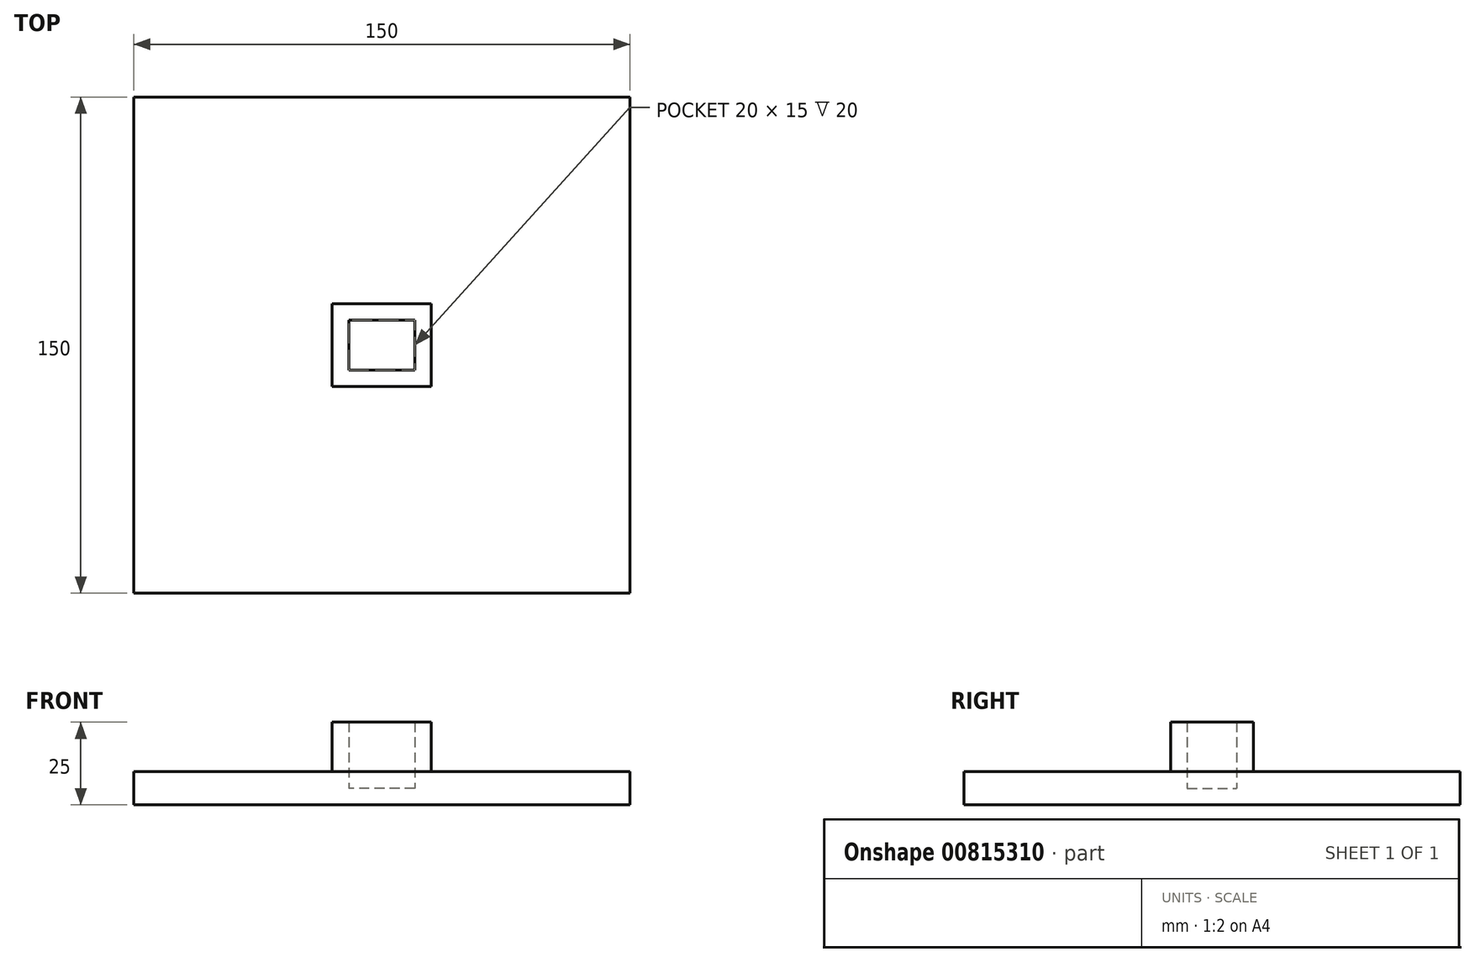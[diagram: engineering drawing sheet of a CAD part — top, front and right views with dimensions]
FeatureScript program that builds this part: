
annotation { "Feature Type Name" : "Feature", "Feature Type Description" : "" }
export const myFeature = defineFeature(function(context is Context, id is Id, definition is map)
    precondition{}
    {
        {
            var Q0;
            Q0=qCreatedBy(makeId("Top.planeOp"),FACE);
            var sketch = newSketch(context, id + "F0", { "sketchPlane" : qUnion([Q0])});
            skLineSegment(sketch, "E0.bottom", {"start": v(42.35, 98.82) * mm, "end": v(192.35, 98.82) * mm});
            skLineSegment(sketch, "E0.top", {"start": v(42.35, -51.18) * mm, "end": v(192.35, -51.18) * mm});
            skLineSegment(sketch, "E0.left", {"start": v(42.35, 98.82) * mm, "end": v(42.35, -51.18) * mm});
            skLineSegment(sketch, "E0.right", {"start": v(192.35, 98.82) * mm, "end": v(192.35, -51.18) * mm});
            skLineSegment(sketch, "E1", {"start": v(42.35, 98.82) * mm, "end": v(192.35, -51.18) * mm});
            skLineSegment(sketch, "E2", {"start": v(192.35, 98.82) * mm, "end": v(42.35, -51.18) * mm});
            skLineSegment(sketch, "E3.bottom", {"start": v(127.35, 16.32) * mm, "end": v(107.35, 16.32) * mm});
            skLineSegment(sketch, "E3.top", {"start": v(127.35, 31.32) * mm, "end": v(107.35, 31.32) * mm});
            skLineSegment(sketch, "E3.left", {"start": v(127.35, 16.32) * mm, "end": v(127.35, 31.32) * mm});
            skLineSegment(sketch, "E3.right", {"start": v(107.35, 16.32) * mm, "end": v(107.35, 31.32) * mm});
            skPoint(sketch, "E3.middle", {"position": v(117.35, 23.82) * mm});
            skSolve(sketch);
        }
        {
            var Q0;
            {var subQ1=sQuery(id+"F0.wireOp",EDGE,"E0.left");Q0=makeQuery(id+"F0.imprint","IMPRINT",FACE,{"disambiguationData":[TD([[makeQuery(id+"F0.imprint","IMPRINT",EDGE,{"derivedFrom":subQ1}),1.0]])]});}
            var Q1;
            {var subQ0=sQuery(id+"F0.wireOp",EDGE,"E0.bottom");Q1=makeQuery(id+"F0.imprint","IMPRINT",FACE,{"disambiguationData":[TD([[makeQuery(id+"F0.imprint","IMPRINT",EDGE,{"derivedFrom":subQ0}),-1.0]])]});}
            var Q2;
            {var subQ4=sQuery(id+"F0.wireOp",EDGE,"E0.right");Q2=makeQuery(id+"F0.imprint","IMPRINT",FACE,{"disambiguationData":[TD([[makeQuery(id+"F0.imprint","IMPRINT",EDGE,{"derivedFrom":subQ4}),-1.0]])]});}
            var Q3;
            {var subQ0=sQuery(id+"F0.wireOp",EDGE,"E0.top");Q3=makeQuery(id+"F0.imprint","IMPRINT",FACE,{"disambiguationData":[TD([[makeQuery(id+"F0.imprint","IMPRINT",EDGE,{"derivedFrom":subQ0}),1.0]])]});}
            extrude(context, id + "F1", {"entities" : qUnion([Q0, Q1, Q2, Q3]), "depth" : 10 * mm, "offsetDistance" : 25 * mm});
        }
        {
            var Q0;
            Q0=makeQuery(id+"F1.opExtrude","CAP_FACE",FACE,{"disambiguationData":[OSD([sQuery(id+"F0.wireOp",EDGE,"E0.bottom"),sQuery(id+"F0.wireOp",EDGE,"E0.top"),sQuery(id+"F0.wireOp",EDGE,"E0.left"),sQuery(id+"F0.wireOp",EDGE,"E0.right"),sQuery(id+"F0.wireOp",EDGE,"E3.bottom"),sQuery(id+"F0.wireOp",EDGE,"E3.top"),sQuery(id+"F0.wireOp",EDGE,"E3.left"),sQuery(id+"F0.wireOp",EDGE,"E3.right")])],"isStart":false});
            var sketch = newSketch(context, id + "F2", { "sketchPlane" : qUnion([Q0])});
            skLineSegment(sketch, "E4", {"start": v(107.35, 16.32) * mm, "end": v(127.35, 31.32) * mm});
            skLineSegment(sketch, "E5", {"start": v(127.35, 31.32) * mm, "end": v(107.35, 31.32) * mm});
            skLineSegment(sketch, "E6", {"start": v(107.35, 31.32) * mm, "end": v(127.35, 16.32) * mm});
            skLineSegment(sketch, "E7.bottom", {"start": v(132.35, 11.32) * mm, "end": v(102.35, 11.32) * mm});
            skLineSegment(sketch, "E7.top", {"start": v(132.35, 36.32) * mm, "end": v(102.35, 36.32) * mm});
            skLineSegment(sketch, "E7.left", {"start": v(132.35, 11.32) * mm, "end": v(132.35, 36.32) * mm});
            skLineSegment(sketch, "E7.right", {"start": v(102.35, 11.32) * mm, "end": v(102.35, 36.32) * mm});
            skPoint(sketch, "E7.middle", {"position": v(117.35, 23.82) * mm});
            skSolve(sketch);
        }
        {
            var Q0;
            Q0=makeQuery(id+"F2.imprint","IMPRINT",FACE,{"disambiguationData":[TD([[makeQuery(id+"F2.imprint","IMPRINT",EDGE,{"derivedFrom":sQuery(id+"F2.wireOp",EDGE,"E5")}),-1.0]])]});
            extrude(context, id + "F3", {"entities" : qUnion([Q0]), "operationType" : NewBodyOperationType.ADD, "depth" : 15 * mm, "offsetDistance" : 25 * mm});
        }
        {
            var Q0;
            {var subQ0=sQuery(id+"F0.wireOp",EDGE,"E3.left");Q0=makeQuery(id+"F0.imprint","IMPRINT",FACE,{"disambiguationData":[TD([[makeQuery(id+"F0.imprint","IMPRINT",EDGE,{"derivedFrom":subQ0}),1.0]])]});}
            var Q1;
            {var subQ0=sQuery(id+"F0.wireOp",EDGE,"E3.top");var subQ1=sQuery(id+"F0.wireOp",EDGE,"E1");var subQ2=makeQuery(id+"F0.imprint","INTERSECT",VERTEX,{"derivedFrom":[subQ1,subQ0]});Q1=makeQuery(id+"F0.imprint","IMPRINT",FACE,{"disambiguationData":[TD([[makeQuery(id+"F0.imprint","IMPRINT",EDGE,{"disambiguationData":[TD([[subQ2,-1.0]])],"derivedFrom":subQ1}),1.0]])]});}
            var Q2;
            {var subQ0=sQuery(id+"F0.wireOp",EDGE,"E3.right");Q2=makeQuery(id+"F0.imprint","IMPRINT",FACE,{"disambiguationData":[TD([[makeQuery(id+"F0.imprint","IMPRINT",EDGE,{"derivedFrom":subQ0}),-1.0]])]});}
            var Q3;
            {var subQ0=sQuery(id+"F0.wireOp",EDGE,"E2");var subQ1=sQuery(id+"F0.wireOp",EDGE,"E1");var subQ2=makeQuery(id+"F0.imprint","INTERSECT",VERTEX,{"derivedFrom":[subQ1,subQ0]});Q3=makeQuery(id+"F0.imprint","IMPRINT",FACE,{"disambiguationData":[TD([[makeQuery(id+"F0.imprint","IMPRINT",EDGE,{"disambiguationData":[TD([[subQ2,-1.0]])],"derivedFrom":subQ1}),-1.0]])]});}
            extrude(context, id + "F4", {"entities" : qUnion([Q0, Q1, Q2, Q3]), "operationType" : NewBodyOperationType.ADD, "depth" : 5 * mm, "offsetDistance" : 25 * mm});
        }
    });
